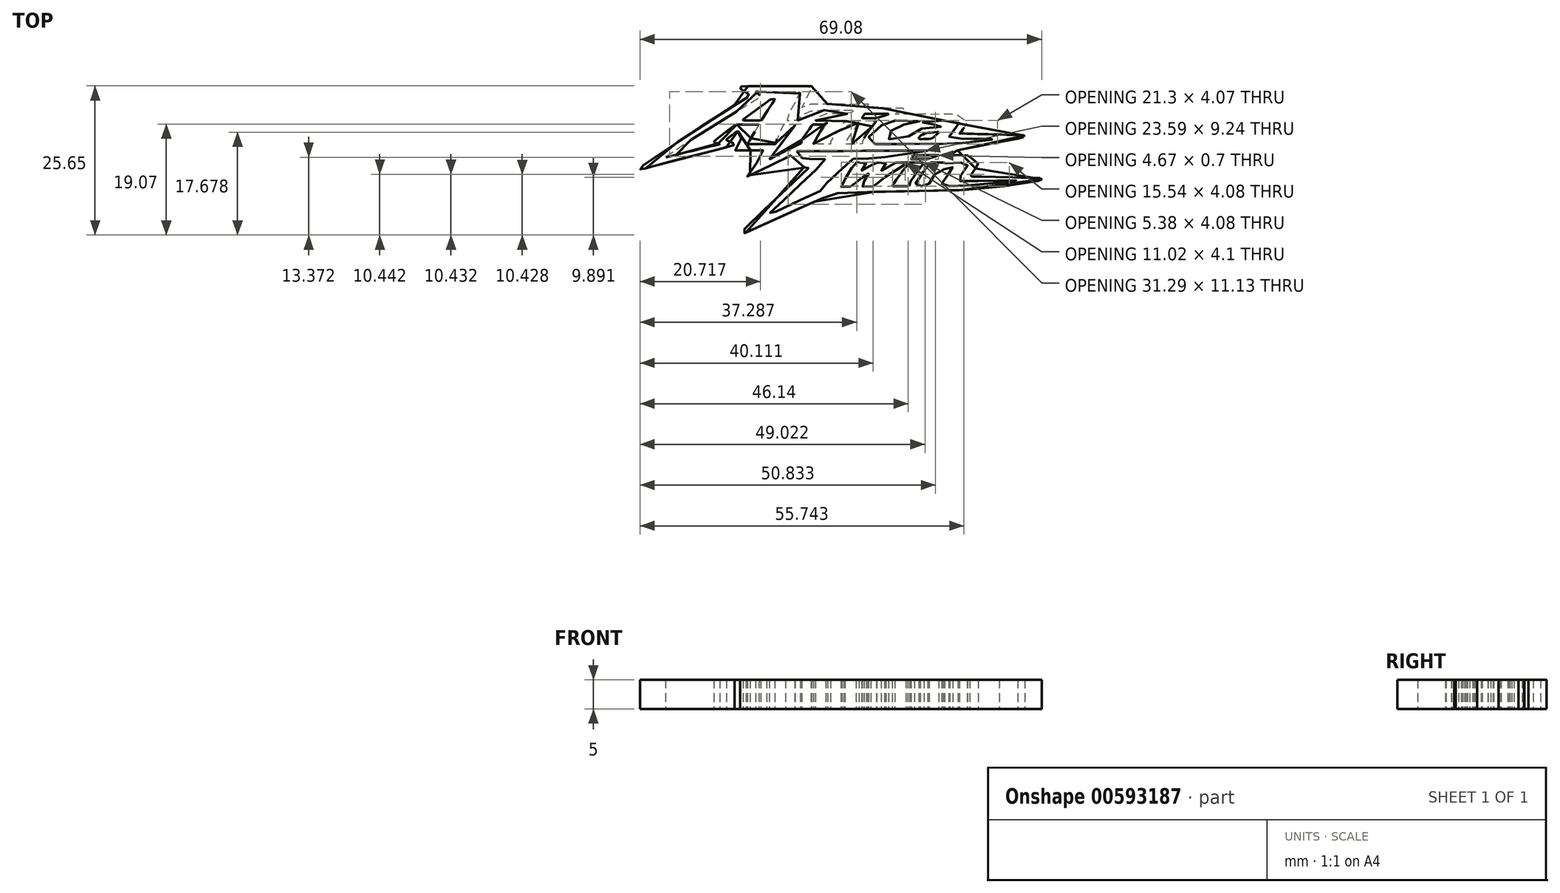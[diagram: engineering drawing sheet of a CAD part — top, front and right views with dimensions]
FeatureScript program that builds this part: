
annotation { "Feature Type Name" : "Feature", "Feature Type Description" : "" }
export const myFeature = defineFeature(function(context is Context, id is Id, definition is map)
    precondition{}
    {
        {
            var Q0;
            Q0=qCreatedBy(makeId("Top.planeOp"),FACE);
            var sketch = newSketch(context, id + "F0", { "sketchPlane" : qUnion([Q0])});
            skFitSpline(sketch, "E0", {"points": [v(-31.44, 20.71) * mm, v(-28.3, 20.77) * mm, v(-24.77, 20.79) * mm, v(-21.15, 20.83) * mm, v(-17.69, 20.85) * mm, v(-13.86, 20.87) * mm, v(-10.72, 20.85) * mm, v(-9.64, 20.77) * mm, v(-9.44, 20.67) * mm, v(-9.36, 20.45) * mm, v(-9.71, 19.84) * mm, v(-10.66, 17.85) * mm, v(-11.86, 15.37) * mm, v(-12.62, 13.83) * mm, v(-12.87, 13.46) * mm, v(-12.36, 13.66) * mm, v(-10.48, 14.38) * mm, v(-9.76, 14.62) * mm, v(-8.3, 14.67) * mm, v(-0.15, 14.62) * mm, v(8.5, 14.6) * mm, v(10.43, 14.62) * mm, v(10.86, 14.5) * mm, v(10.52, 14.24) * mm, v(9.13, 13.52) * mm, v(8.62, 13.24) * mm, v(9.3, 13.23) * mm, v(13.38, 13.2) * mm, v(17.6, 13.21) * mm, v(21.22, 13.2) * mm, v(22.36, 13.21) * mm, v(22.72, 13.17) * mm, v(22.9, 13.05) * mm, v(22.8, 12.92) * mm, v(22, 12.5) * mm, v(19.52, 11.38) * mm, v(19.17, 11.22) * mm, v(19.52, 11.18) * mm, v(21.42, 11.2) * mm, v(27.58, 11.15) * mm, v(35.7, 11.2) * mm, v(39.4, 11.2) * mm, v(39.96, 11.2) * mm, v(40.45, 11.02) * mm, v(41.07, 10.67) * mm, v(43.51, 8.93) * mm, v(43.88, 8.62) * mm, v(44.1, 8.35) * mm, v(44.07, 8.16) * mm, v(43.88, 7.78) * mm, v(43.2, 6.82) * mm, v(41.7, 4.75) * mm, v(41.4, 4.44) * mm, v(41.8, 4.44) * mm, v(46.51, 4.34) * mm, v(54.03, 4.15) * mm, v(62.87, 3.9) * mm, v(63.5, 3.86) * mm, v(63.75, 3.7) * mm, v(63.8, 3.5) * mm, v(63.56, 3.27) * mm, v(62.78, 3.02) * mm, v(61.33, 2.68) * mm, v(50.17, 0.51) * mm, v(48.29, 0.16) * mm, v(43.82, -0.7) * mm, v(41.17, -1.17) * mm, v(40.71, -1.31) * mm, v(40.3, -1.52) * mm, v(38.4, -2.7) * mm, v(38.08, -2.95) * mm, v(38.48, -2.96) * mm, v(42.95, -2.96) * mm, v(43.87, -3) * mm, v(44.42, -3.15) * mm, v(45.17, -3.73) * mm, v(47.66, -5.83) * mm, v(47.85, -6) * mm, v(47.88, -6.2) * mm, v(47.65, -6.53) * mm, v(45.18, -9.97) * mm, v(44.95, -10.32) * mm, v(45.44, -10.34) * mm, v(49.6, -10.42) * mm, v(60.85, -10.66) * mm, v(68.92, -10.88) * mm, v(69.35, -10.9) * mm, v(69.58, -11.06) * mm, v(69.63, -11.3) * mm, v(69.4, -11.5) * mm, v(68.72, -11.77) * mm, v(67.84, -11.94) * mm, v(61.37, -13.03) * mm, v(54.69, -13.9) * mm, v(46.25, -14.7) * mm, v(39.74, -15.1) * mm, v(35.06, -15.2) * mm, v(29.92, -15.28) * mm, v(24.8, -15.36) * mm, v(22.23, -15.43) * mm, v(14.78, -15.56) * mm, v(7.73, -15.76) * mm, v(1.76, -15.96) * mm, v(-0.16, -16.08) * mm, v(-1.23, -16.17) * mm, v(-1.7, -16.22) * mm, v(-2.2, -16.36) * mm, v(-3.15, -16.73) * mm, v(-5.36, -17.68) * mm, v(-8.55, -19) * mm, v(-11.16, -20.13) * mm, v(-15.96, -22.24) * mm, v(-19.22, -23.72) * mm, v(-24.73, -26.23) * mm, v(-29.57, -28.5) * mm, v(-31.83, -29.52) * mm, v(-33.6, -30.36) * mm, v(-33.79, -30.44) * mm, v(-33.93, -30.42) * mm, v(-34.06, -30.3) * mm, v(-34.08, -30.09) * mm, v(-33.96, -29.86) * mm, v(-33.08, -28.95) * mm, v(-30.44, -26.24) * mm, v(-27.52, -23.44) * mm, v(-24.82, -20.86) * mm, v(-21.12, -17.38) * mm, v(-17.92, -14.4) * mm, v(-14.38, -11.08) * mm, v(-11, -7.9) * mm, v(-9.75, -6.67) * mm, v(-9.62, -6.52) * mm, v(-9.85, -6.53) * mm, v(-10.86, -6.51) * mm, v(-10.98, -6.5) * mm, v(-11.63, -6.92) * mm, v(-11.95, -7.17) * mm, v(-12.1, -7.28) * mm, v(-12.24, -7.26) * mm, v(-12.64, -6.9) * mm, v(-15.8, -3.99) * mm, v(-16.66, -3.2) * mm, v(-16.75, -3.13) * mm, v(-16.94, -3.2) * mm, v(-19.02, -4.23) * mm, v(-21.54, -5.46) * mm, v(-26.34, -7.81) * mm, v(-30.32, -9.78) * mm, v(-31.48, -10.3) * mm, v(-31.67, -10.36) * mm, v(-31.85, -10.36) * mm, v(-31.94, -10.3) * mm, v(-32.02, -10.18) * mm, v(-31.91, -9.98) * mm, v(-31.16, -9.08) * mm, v(-27.72, -4.86) * mm, v(-25.69, -2.27) * mm, v(-25.03, -1.4) * mm, v(-24.98, -1.27) * mm, v(-25.27, -1.27) * mm, v(-30.34, -1.33) * mm, v(-34.83, -1.37) * mm, v(-35.61, -1.39) * mm, v(-35.8, -1.35) * mm, v(-35.92, -1.19) * mm, v(-35.92, -0.93) * mm, v(-35.79, -0.6) * mm, v(-35.04, 0.69) * mm, v(-33.92, 2.35) * mm, v(-32.9, 3.85) * mm, v(-31.97, 5.16) * mm, v(-31.97, 5.22) * mm, v(-32.3, 5.21) * mm, v(-34.88, 5.21) * mm, v(-34.96, 5.2) * mm, v(-35.2, 5.11) * mm, v(-36.44, 4.2) * mm, v(-38.05, 2.99) * mm, v(-38.72, 2.42) * mm, v(-38.81, 2.3) * mm, v(-38.79, 2.2) * mm, v(-38.64, 2.13) * mm, v(-38.37, 2) * mm, v(-36.75, 1.34) * mm, v(-36.2, 1.05) * mm, v(-35.96, 0.86) * mm, v(-35.85, 0.75) * mm, v(-35.93, 0.63) * mm, v(-36.35, 0.46) * mm, v(-37.36, 0.16) * mm, v(-39.12, -0.35) * mm, v(-42.53, -1.26) * mm, v(-47.35, -2.49) * mm, v(-52.88, -3.85) * mm, v(-58.58, -5.28) * mm, v(-64.61, -6.93) * mm, v(-67.43, -7.8) * mm, v(-67.74, -7.88) * mm, v(-68.03, -7.92) * mm, v(-68.31, -7.88) * mm, v(-68.5, -7.72) * mm, v(-68.5, -7.48) * mm, v(-68.17, -7.1) * mm, v(-67.4, -6.57) * mm, v(-64.48, -4.56) * mm, v(-61.76, -2.71) * mm, v(-58.36, -0.4) * mm, v(-55.05, 1.82) * mm, v(-52.23, 3.7) * mm, v(-49.26, 5.65) * mm, v(-46.62, 7.37) * mm, v(-43.48, 9.42) * mm, v(-40.62, 11.22) * mm, v(-37.84, 13) * mm, v(-34.36, 15.19) * mm, v(-31.23, 17.12) * mm, v(-30.7, 17.45) * mm, v(-30.59, 17.53) * mm, v(-30.7, 17.64) * mm, v(-31.88, 18.45) * mm, v(-33.47, 19.51) * mm, v(-34.2, 20.02) * mm, v(-34.3, 20.16) * mm, v(-34.33, 20.32) * mm, v(-34.21, 20.45) * mm, v(-33.86, 20.55) * mm, v(-33.08, 20.64) * mm, v(-32.38, 20.68) * mm, v(-31.44, 20.71) * mm]});
            skFitSpline(sketch, "E1", {"points": [v(-27.94, 18.83) * mm, v(-25.36, 18.85) * mm, v(-22.64, 18.83) * mm, v(-20.72, 18.82) * mm, v(-18.67, 18.83) * mm, v(-15.9, 18.83) * mm, v(-14.1, 18.83) * mm, v(-13.7, 18.83) * mm, v(-13.59, 18.81) * mm, v(-13.4, 18.65) * mm, v(-13.37, 18.58) * mm, v(-13.39, 18.45) * mm, v(-13.7, 17.85) * mm, v(-14.8, 15.8) * mm, v(-15.84, 13.94) * mm, v(-17.05, 11.71) * mm, v(-17.96, 9.93) * mm, v(-18.38, 9.15) * mm, v(-18.43, 9.04) * mm, v(-18.36, 8.98) * mm, v(-18.19, 8.98) * mm, v(-16.4, 8.98) * mm, v(-14.38, 9) * mm, v(-14.13, 9) * mm, v(-14, 9) * mm, v(-13.85, 9.16) * mm, v(-13.33, 9.76) * mm, v(-12.75, 10.5) * mm, v(-12.45, 10.91) * mm, v(-12.36, 11.02) * mm, v(-12.14, 11.15) * mm, v(-11.18, 11.59) * mm, v(-10.62, 11.83) * mm, v(-9.52, 12.26) * mm, v(-9.14, 12.38) * mm, v(-8.8, 12.46) * mm, v(-8.18, 12.48) * mm, v(-6.37, 12.48) * mm, v(-3.07, 12.5) * mm, v(0.47, 12.48) * mm, v(4, 12.5) * mm, v(5.57, 12.5) * mm, v(5.7, 12.47) * mm, v(5.77, 12.4) * mm, v(5.78, 12.33) * mm, v(5.63, 12.27) * mm, v(5.55, 12.22) * mm, v(4.72, 11.87) * mm, v(3.96, 11.55) * mm, v(3.4, 11.36) * mm, v(3.14, 11.28) * mm, v(2.72, 11.26) * mm, v(1.7, 11.25) * mm, v(-1.97, 11.24) * mm, v(-4.14, 11.26) * mm, v(-4.41, 11.24) * mm, v(-4.77, 11.17) * mm, v(-5.2, 10.98) * mm, v(-5.83, 10.72) * mm, v(-6.38, 10.48) * mm, v(-6.7, 10.32) * mm, v(-7.08, 10.03) * mm, v(-7.67, 9.55) * mm, v(-8.12, 9.15) * mm, v(-8.16, 9.05) * mm, v(-8.07, 8.98) * mm, v(-7.9, 9) * mm, v(-5.92, 9) * mm, v(-2.75, 8.97) * mm, v(0.26, 8.98) * mm, v(1.36, 8.99) * mm, v(1.5, 8.97) * mm, v(1.57, 8.94) * mm, v(1.6, 8.87) * mm, v(1.57, 8.8) * mm, v(1.47, 8.68) * mm, v(1.1, 8.12) * mm, v(1.03, 8.03) * mm, v(1.1, 7.95) * mm, v(1.2, 7.98) * mm, v(1.46, 8.12) * mm, v(2.51, 8.65) * mm, v(3.07, 8.87) * mm, v(3.35, 8.95) * mm, v(3.77, 8.97) * mm, v(5.54, 8.99) * mm, v(7.3, 8.97) * mm, v(9.54, 8.98) * mm, v(12.54, 8.99) * mm, v(12.68, 8.98) * mm, v(12.77, 8.95) * mm, v(12.82, 8.88) * mm, v(12.8, 8.83) * mm, v(12.7, 8.7) * mm, v(12.39, 8.3) * mm, v(11.56, 7.18) * mm, v(10.72, 6) * mm, v(9.85, 4.83) * mm, v(9.03, 3.65) * mm, v(8.33, 2.51) * mm, v(8.12, 2.16) * mm, v(7.97, 1.78) * mm, v(7.9, 1.55) * mm, v(7.9, 1.26) * mm, v(7.92, 1.1) * mm, v(7.96, 1.01) * mm, v(7.95, 0.92) * mm, v(7.88, 0.85) * mm, v(7.64, 0.85) * mm, v(7.26, 0.86) * mm, v(5.58, 0.85) * mm, v(4, 0.85) * mm, v(2.88, 0.84) * mm, v(2.23, 0.83) * mm, v(2.14, 0.87) * mm, v(2.05, 0.92) * mm, v(2, 1) * mm, v(2, 1.11) * mm, v(2.11, 1.26) * mm, v(2.32, 1.6) * mm, v(3.29, 3.02) * mm, v(4.07, 4.21) * mm, v(4.93, 5.49) * mm, v(5.7, 6.66) * mm, v(6.27, 7.5) * mm, v(6.62, 8.04) * mm, v(6.77, 8.25) * mm, v(6.84, 8.35) * mm, v(6.8, 8.39) * mm, v(6.75, 8.36) * mm, v(6.6, 8.3) * mm, v(6.12, 8.06) * mm, v(5.7, 7.86) * mm, v(5.39, 7.68) * mm, v(5.17, 7.57) * mm, v(4.7, 7.51) * mm, v(4.02, 7.45) * mm, v(3.55, 7.4) * mm, v(3.34, 7.36) * mm, v(3.18, 7.3) * mm, v(2.6, 7.04) * mm, v(1.12, 6.3) * mm, v(-0.07, 5.6) * mm, v(-0.36, 5.41) * mm, v(-0.58, 5.19) * mm, v(-0.91, 4.83) * mm, v(-1.73, 3.65) * mm, v(-2.5, 2.48) * mm, v(-2.83, 1.87) * mm, v(-2.94, 1.49) * mm, v(-2.97, 1.2) * mm, v(-2.94, 0.93) * mm, v(-2.93, 0.86) * mm, v(-3.01, 0.83) * mm, v(-3.3, 0.84) * mm, v(-4.13, 0.84) * mm, v(-6.48, 0.84) * mm, v(-8.4, 0.84) * mm, v(-8.54, 0.85) * mm, v(-8.67, 0.9) * mm, v(-8.74, 0.95) * mm, v(-8.78, 1.04) * mm, v(-8.74, 1.15) * mm, v(-8.6, 1.33) * mm, v(-8.25, 1.87) * mm, v(-7.37, 3.17) * mm, v(-6.3, 4.76) * mm, v(-5.43, 6.05) * mm, v(-4.42, 7.53) * mm, v(-4.17, 7.86) * mm, v(-3.95, 8.14) * mm, v(-3.91, 8.2) * mm, v(-3.93, 8.22) * mm, v(-3.98, 8.25) * mm, v(-4.12, 8.19) * mm, v(-4.58, 7.97) * mm, v(-4.8, 7.86) * mm, v(-5.04, 7.75) * mm, v(-5.15, 7.68) * mm, v(-5.28, 7.57) * mm, v(-5.41, 7.57) * mm, v(-6.5, 7.58) * mm, v(-7.44, 7.6) * mm, v(-8.45, 7.58) * mm, v(-8.72, 7.59) * mm, v(-8.86, 7.58) * mm, v(-9.02, 7.53) * mm, v(-9.2, 7.4) * mm, v(-9.4, 7.17) * mm, v(-10.12, 6.14) * mm, v(-10.87, 5.13) * mm, v(-12.03, 3.51) * mm, v(-12.67, 2.61) * mm, v(-12.94, 2.1) * mm, v(-13, 1.78) * mm, v(-12.98, 1.39) * mm, v(-12.98, 1.24) * mm, v(-12.98, 1.18) * mm, v(-13.05, 1.12) * mm, v(-13.57, 0.85) * mm, v(-16.05, -0.34) * mm, v(-18.68, -1.62) * mm, v(-21.07, -2.85) * mm, v(-23.2, -4.06) * mm, v(-23.86, -4.42) * mm, v(-23.99, -4.46) * mm, v(-23.97, -4.38) * mm, v(-23.9, -4.3) * mm, v(-23.55, -3.86) * mm, v(-22.4, -2.47) * mm, v(-21.58, -1.48) * mm, v(-21.03, -0.75) * mm, v(-20.06, 0.46) * mm, v(-19.46, 1.23) * mm, v(-17.66, 3.63) * mm, v(-15.85, 6.13) * mm, v(-15.14, 7.15) * mm, v(-15.08, 7.24) * mm, v(-15.1, 7.37) * mm, v(-15.22, 7.48) * mm, v(-15.39, 7.55) * mm, v(-15.54, 7.59) * mm, v(-16.37, 7.58) * mm, v(-18.12, 7.59) * mm, v(-18.98, 7.59) * mm, v(-19.06, 7.6) * mm, v(-19.12, 7.57) * mm, v(-19.19, 7.46) * mm, v(-19.71, 6.32) * mm, v(-20.6, 4.39) * mm, v(-21.2, 3) * mm, v(-21.35, 2.6) * mm, v(-21.5, 2.03) * mm, v(-21.7, 1.2) * mm, v(-21.75, 1.05) * mm, v(-21.8, 0.96) * mm, v(-21.91, 0.89) * mm, v(-22.11, 0.86) * mm, v(-22.6, 0.87) * mm, v(-25.77, 0.85) * mm, v(-28.27, 0.82) * mm, v(-30.4, 0.78) * mm, v(-31.24, 0.76) * mm, v(-31.37, 0.78) * mm, v(-31.45, 0.84) * mm, v(-31.48, 0.93) * mm, v(-31.44, 1.05) * mm, v(-31.24, 1.34) * mm, v(-30.56, 2.5) * mm, v(-30.22, 3.09) * mm, v(-29.67, 4.03) * mm, v(-29.06, 4.98) * mm, v(-28.3, 6.24) * mm, v(-27.74, 7.1) * mm, v(-27.63, 7.3) * mm, v(-27.6, 7.44) * mm, v(-27.66, 7.53) * mm, v(-27.78, 7.57) * mm, v(-28.8, 7.57) * mm, v(-32.18, 7.55) * mm, v(-34.64, 7.59) * mm, v(-35.2, 7.6) * mm, v(-35.48, 7.55) * mm, v(-35.8, 7.42) * mm, v(-36.13, 7.21) * mm, v(-36.46, 6.95) * mm, v(-37.18, 6.43) * mm, v(-39.8, 4.34) * mm, v(-41.94, 2.73) * mm, v(-42.38, 2.35) * mm, v(-42.88, 1.92) * mm, v(-43.03, 1.74) * mm, v(-43.06, 1.59) * mm, v(-42.98, 1.45) * mm, v(-42.76, 1.34) * mm, v(-41.95, 1.15) * mm, v(-41.37, 1.02) * mm, v(-41.17, 0.92) * mm, v(-41.08, 0.85) * mm, v(-41.08, 0.78) * mm, v(-41.16, 0.73) * mm, v(-41.47, 0.67) * mm, v(-41.8, 0.57) * mm, v(-44.01, 0.07) * mm, v(-45.43, -0.27) * mm, v(-48.03, -0.9) * mm, v(-51.88, -1.85) * mm, v(-54.82, -2.56) * mm, v(-58.1, -3.36) * mm, v(-59.13, -3.63) * mm, v(-59.46, -3.7) * mm, v(-59.64, -3.68) * mm, v(-59.65, -3.61) * mm, v(-59.58, -3.5) * mm, v(-59.4, -3.34) * mm, v(-58.34, -2.59) * mm, v(-56.94, -1.67) * mm, v(-54.92, -0.34) * mm, v(-53.9, 0.34) * mm, v(-51.67, 1.76) * mm, v(-49.53, 3.14) * mm, v(-48.87, 3.58) * mm, v(-48.73, 3.67) * mm, v(-47.04, 4.75) * mm, v(-44.1, 6.6) * mm, v(-41.55, 8.22) * mm, v(-38.39, 10.15) * mm, v(-35.9, 11.7) * mm, v(-33.5, 13.18) * mm, v(-30.87, 14.8) * mm, v(-27.86, 16.62) * mm, v(-26.98, 17.22) * mm, v(-26.93, 17.35) * mm, v(-26.94, 17.46) * mm, v(-27.02, 17.57) * mm, v(-27.47, 17.84) * mm, v(-27.98, 18.15) * mm, v(-28.6, 18.54) * mm, v(-28.65, 18.63) * mm, v(-28.66, 18.74) * mm, v(-28.59, 18.83) * mm, v(-28.36, 18.84) * mm, v(-27.94, 18.83) * mm]});
            skFitSpline(sketch, "E2", {"points": [v(-22.35, 15.82) * mm, v(-22.84, 15.12) * mm, v(-23.43, 14.18) * mm, v(-24.2, 13.02) * mm, v(-24.91, 11.9) * mm, v(-26, 10.2) * mm, v(-26.5, 9.37) * mm, v(-26.57, 9.25) * mm, v(-26.7, 9.13) * mm, v(-26.97, 9) * mm, v(-27.15, 8.98) * mm, v(-27.78, 8.98) * mm, v(-30.38, 8.98) * mm, v(-32.52, 8.99) * mm, v(-32.62, 8.99) * mm, v(-32.84, 9) * mm, v(-32.96, 9.05) * mm, v(-33.05, 9.11) * mm, v(-33.07, 9.23) * mm, v(-33, 9.36) * mm, v(-32.83, 9.5) * mm, v(-32.07, 10.06) * mm, v(-30.65, 11.06) * mm, v(-29.08, 12.22) * mm, v(-28.27, 12.82) * mm, v(-26.87, 13.82) * mm, v(-25.71, 14.67) * mm, v(-24.21, 15.76) * mm, v(-23.77, 16.09) * mm, v(-23.6, 16.2) * mm, v(-23.35, 16.27) * mm, v(-23.1, 16.3) * mm, v(-22.62, 16.3) * mm, v(-22.22, 16.32) * mm, v(-22.13, 16.28) * mm, v(-22.11, 16.21) * mm, v(-22.15, 16.15) * mm, v(-22.25, 16) * mm, v(-22.35, 15.82) * mm]});
            skFitSpline(sketch, "E3", {"points": [v(12, 11.25) * mm, v(14.22, 11.25) * mm, v(16.62, 11.24) * mm, v(16.78, 11.24) * mm, v(16.86, 11.21) * mm, v(16.96, 11.13) * mm, v(16.95, 11.09) * mm, v(16.84, 11.03) * mm, v(16.26, 10.83) * mm, v(14.13, 10.16) * mm, v(13.26, 9.87) * mm, v(13.01, 9.8) * mm, v(12.88, 9.79) * mm, v(12.62, 9.75) * mm, v(12, 9.74) * mm, v(9.53, 9.74) * mm, v(8.25, 9.74) * mm, v(8.1, 9.75) * mm, v(8, 9.8) * mm, v(7.93, 9.9) * mm, v(7.96, 10) * mm, v(8.08, 10.19) * mm, v(8.3, 10.52) * mm, v(8.66, 11.04) * mm, v(8.75, 11.14) * mm, v(8.92, 11.2) * mm, v(9.11, 11.22) * mm, v(9.68, 11.23) * mm, v(12, 11.25) * mm]});
            skFitSpline(sketch, "E4", {"points": [v(19.36, 8.99) * mm, v(22.68, 8.97) * mm, v(26.98, 8.98) * mm, v(27.74, 8.98) * mm, v(27.87, 8.95) * mm, v(27.9, 8.9) * mm, v(27.9, 8.85) * mm, v(27.81, 8.79) * mm, v(26.72, 8.05) * mm, v(26.31, 7.8) * mm, v(26.14, 7.7) * mm, v(25.95, 7.64) * mm, v(25.68, 7.6) * mm, v(25.22, 7.58) * mm, v(23.34, 7.58) * mm, v(22.34, 7.58) * mm, v(22.07, 7.58) * mm, v(21.9, 7.56) * mm, v(21.57, 7.43) * mm, v(20.7, 7.11) * mm, v(19.5, 6.6) * mm, v(19.23, 6.46) * mm, v(18.91, 6.25) * mm, v(18.35, 5.78) * mm, v(16.43, 4.07) * mm, v(15.81, 3.42) * mm, v(15.68, 3.27) * mm, v(15.64, 3.16) * mm, v(15.67, 3) * mm, v(15.77, 2.85) * mm, v(16.02, 2.67) * mm, v(16.3, 2.56) * mm, v(16.65, 2.52) * mm, v(17.73, 2.53) * mm, v(21.55, 2.52) * mm, v(22.6, 2.53) * mm, v(22.94, 2.53) * mm, v(23, 2.53) * mm, v(23.05, 2.6) * mm, v(23.41, 3.02) * mm, v(23.63, 3.26) * mm, v(24.59, 4.23) * mm, v(25.3, 4.9) * mm, v(25.69, 5.2) * mm, v(25.97, 5.35) * mm, v(26.75, 5.64) * mm, v(27.39, 5.85) * mm, v(28.23, 6.08) * mm, v(28.93, 6.15) * mm, v(29.7, 6.23) * mm, v(31.7, 6.4) * mm, v(33.63, 6.54) * mm, v(34.2, 6.6) * mm, v(34.7, 6.66) * mm, v(35.26, 6.83) * mm, v(35.67, 7.05) * mm, v(36.07, 7.23) * mm, v(36.27, 7.4) * mm, v(36.3, 7.48) * mm, v(36.3, 7.54) * mm, v(36.25, 7.57) * mm, v(36.1, 7.57) * mm, v(34.31, 7.56) * mm, v(32.6, 7.56) * mm, v(30.43, 7.56) * mm, v(28.46, 7.56) * mm, v(28.03, 7.55) * mm, v(27.98, 7.56) * mm, v(27.91, 7.6) * mm, v(27.86, 7.67) * mm, v(27.85, 7.73) * mm, v(27.9, 7.8) * mm, v(28.04, 7.9) * mm, v(28.89, 8.5) * mm, v(29.46, 8.87) * mm, v(29.62, 8.94) * mm, v(29.72, 8.98) * mm, v(29.84, 8.99) * mm, v(30.41, 9) * mm, v(32.93, 9) * mm, v(35.39, 8.99) * mm, v(38.86, 8.99) * mm, v(39.63, 8.98) * mm, v(39.87, 8.97) * mm, v(40.04, 8.93) * mm, v(40.22, 8.87) * mm, v(40.42, 8.75) * mm, v(41.05, 8.3) * mm, v(41.22, 8.16) * mm, v(41.28, 8.07) * mm, v(41.3, 7.97) * mm, v(41.27, 7.87) * mm, v(41.14, 7.68) * mm, v(41.01, 7.5) * mm, v(40.1, 6.26) * mm, v(39.1, 4.97) * mm, v(38.1, 3.7) * mm, v(37.82, 3.3) * mm, v(37.74, 3.21) * mm, v(37.71, 3.11) * mm, v(37.74, 3.03) * mm, v(37.83, 2.93) * mm, v(38.07, 2.8) * mm, v(38.36, 2.63) * mm, v(38.56, 2.56) * mm, v(38.7, 2.54) * mm, v(39.3, 2.56) * mm, v(41.81, 2.58) * mm, v(44.71, 2.63) * mm, v(47.11, 2.67) * mm, v(49.35, 2.7) * mm, v(51.41, 2.72) * mm, v(52.93, 2.75) * mm, v(54.17, 2.77) * mm, v(54.89, 2.79) * mm, v(54.96, 2.8) * mm, v(55.02, 2.78) * mm, v(55.05, 2.74) * mm, v(55.03, 2.71) * mm, v(54.96, 2.68) * mm, v(54.82, 2.66) * mm, v(53.2, 2.43) * mm, v(51.02, 2.17) * mm, v(48.66, 1.9) * mm, v(45.26, 1.54) * mm, v(41.9, 1.17) * mm, v(39.22, 0.86) * mm, v(38.78, 0.84) * mm, v(36.51, 0.83) * mm, v(35.17, 0.83) * mm, v(34.5, 0.86) * mm, v(34.22, 0.9) * mm, v(34.05, 0.96) * mm, v(33.78, 1.18) * mm, v(33.61, 1.38) * mm, v(33.52, 1.52) * mm, v(33.42, 1.69) * mm, v(33.38, 1.76) * mm, v(33.36, 1.75) * mm, v(33.27, 1.66) * mm, v(32.95, 1.44) * mm, v(32.42, 1.15) * mm, v(32.03, 0.98) * mm, v(31.5, 0.89) * mm, v(30.58, 0.84) * mm, v(28.38, 0.84) * mm, v(25.63, 0.85) * mm, v(23.37, 0.85) * mm, v(19.81, 0.85) * mm, v(16.57, 0.85) * mm, v(13.2, 0.84) * mm, v(12.09, 0.83) * mm, v(11.79, 0.85) * mm, v(11.35, 1) * mm, v(10.86, 1.32) * mm, v(10.16, 2.03) * mm, v(9.82, 2.45) * mm, v(9.75, 2.63) * mm, v(9.75, 2.76) * mm, v(9.81, 2.9) * mm, v(9.97, 3.08) * mm, v(10.5, 3.63) * mm, v(11.11, 4.23) * mm, v(11.88, 4.94) * mm, v(13, 5.95) * mm, v(14.06, 6.9) * mm, v(14.34, 7.11) * mm, v(14.56, 7.3) * mm, v(15.03, 7.59) * mm, v(15.46, 7.77) * mm, v(16.45, 8.18) * mm, v(17.81, 8.69) * mm, v(18.25, 8.85) * mm, v(18.6, 8.95) * mm, v(18.93, 8.99) * mm, v(19.36, 8.99) * mm]});
            skFitSpline(sketch, "E5", {"points": [v(30.67, 4.75) * mm, v(32.06, 4.83) * mm, v(33.57, 4.98) * mm, v(34.1, 5) * mm, v(34.25, 4.98) * mm, v(34.3, 4.94) * mm, v(34.3, 4.86) * mm, v(34.18, 4.73) * mm, v(33.6, 4.16) * mm, v(32.93, 3.51) * mm, v(32.56, 3.19) * mm, v(32.18, 2.95) * mm, v(31.7, 2.76) * mm, v(31.22, 2.65) * mm, v(30.5, 2.56) * mm, v(28.92, 2.54) * mm, v(27.99, 2.53) * mm, v(27.72, 2.58) * mm, v(27.49, 2.74) * mm, v(27.38, 2.83) * mm, v(27.35, 2.9) * mm, v(27.4, 3.02) * mm, v(27.57, 3.28) * mm, v(27.68, 3.42) * mm, v(27.96, 3.64) * mm, v(28.47, 3.97) * mm, v(29.04, 4.3) * mm, v(29.6, 4.54) * mm, v(30.1, 4.68) * mm, v(30.67, 4.75) * mm]});
            skFitSpline(sketch, "E6", {"points": [v(-14.6, -1.57) * mm, v(-11.2, -1.57) * mm, v(-8.48, -1.56) * mm, v(-4.15, -1.55) * mm, v(-0.76, -1.54) * mm, v(2.28, -1.52) * mm, v(4.75, -1.5) * mm, v(6.58, -1.5) * mm, v(8.88, -1.5) * mm, v(11.94, -1.5) * mm, v(14.7, -1.47) * mm, v(17.8, -1.44) * mm, v(22.1, -1.44) * mm, v(25.9, -1.42) * mm, v(29.15, -1.42) * mm, v(29.99, -1.41) * mm, v(30.42, -1.4) * mm, v(30.5, -1.42) * mm, v(30.5, -1.45) * mm, v(30.4, -1.48) * mm, v(28.76, -1.77) * mm, v(25.05, -2.3) * mm, v(21.95, -2.78) * mm, v(17.9, -3.34) * mm, v(13.88, -3.92) * mm, v(12.93, -4.08) * mm, v(12.07, -4.13) * mm, v(10.14, -4.11) * mm, v(8.64, -4.14) * mm, v(5.74, -4.19) * mm, v(5.16, -4.21) * mm, v(4.9, -4.26) * mm, v(4.63, -4.38) * mm, v(4.25, -4.64) * mm, v(3.5, -5.28) * mm, v(2.2, -6.52) * mm, v(0.46, -8.22) * mm, v(-1.37, -9.96) * mm, v(-3.6, -12.02) * mm, v(-5.55, -13.84) * mm, v(-5.8, -14.14) * mm, v(-6.04, -14.49) * mm, v(-6.16, -14.84) * mm, v(-6.29, -15.13) * mm, v(-6.33, -15.2) * mm, v(-6.42, -15.26) * mm, v(-6.73, -15.42) * mm, v(-10.19, -16.97) * mm, v(-13.51, -18.47) * mm, v(-17.5, -20.35) * mm, v(-21.58, -22.33) * mm, v(-23.28, -23.15) * mm, v(-23.75, -23.37) * mm, v(-23.85, -23.4) * mm, v(-24, -23.4) * mm, v(-24.06, -23.38) * mm, v(-24.08, -23.3) * mm, v(-24.05, -23.2) * mm, v(-23.92, -23.03) * mm, v(-23.24, -22.4) * mm, v(-21.57, -20.8) * mm, v(-20.09, -19.4) * mm, v(-17.6, -17.07) * mm, v(-15.2, -14.85) * mm, v(-13.02, -12.8) * mm, v(-10.94, -10.93) * mm, v(-8.92, -9.02) * mm, v(-6.32, -6.58) * mm, v(-4.75, -5.1) * mm, v(-4.58, -4.88) * mm, v(-4.54, -4.78) * mm, v(-4.56, -4.66) * mm, v(-4.85, -4.45) * mm, v(-5.14, -4.28) * mm, v(-5.25, -4.23) * mm, v(-5.49, -4.24) * mm, v(-7, -4.24) * mm, v(-10.43, -4.22) * mm, v(-11.54, -4.22) * mm, v(-11.66, -4.23) * mm, v(-11.73, -4.25) * mm, v(-11.84, -4.36) * mm, v(-11.98, -4.47) * mm, v(-12.05, -4.5) * mm, v(-12.1, -4.49) * mm, v(-12.23, -4.4) * mm, v(-12.56, -4.1) * mm, v(-14.16, -2.73) * mm, v(-15.13, -1.84) * mm, v(-15.2, -1.76) * mm, v(-15.23, -1.66) * mm, v(-15.19, -1.6) * mm, v(-15.1, -1.56) * mm, v(-14.6, -1.57) * mm]});
            skFitSpline(sketch, "E7", {"points": [v(6.07, -5.46) * mm, v(8.68, -5.48) * mm, v(9.15, -5.5) * mm, v(9.27, -5.5) * mm, v(9.33, -5.53) * mm, v(9.36, -5.6) * mm, v(9.32, -5.69) * mm, v(9.2, -5.9) * mm, v(8.52, -6.99) * mm, v(8.03, -7.79) * mm, v(7.8, -8.15) * mm, v(7.77, -8.25) * mm, v(7.78, -8.35) * mm, v(7.86, -8.41) * mm, v(8, -8.35) * mm, v(8.57, -7.98) * mm, v(9.33, -7.52) * mm, v(10.97, -6.48) * mm, v(11.65, -6.02) * mm, v(12.27, -5.64) * mm, v(12.43, -5.55) * mm, v(12.66, -5.5) * mm, v(13.2, -5.47) * mm, v(14, -5.48) * mm, v(15.85, -5.48) * mm, v(16.05, -5.52) * mm, v(16.1, -5.56) * mm, v(16.14, -5.64) * mm, v(16.06, -5.78) * mm, v(15.87, -6.06) * mm, v(15.23, -7.14) * mm, v(14.78, -7.84) * mm, v(14.57, -8.2) * mm, v(14.51, -8.3) * mm, v(14.52, -8.4) * mm, v(14.6, -8.43) * mm, v(14.8, -8.31) * mm, v(15.52, -7.85) * mm, v(16.5, -7.26) * mm, v(17.29, -6.78) * mm, v(18.2, -6.26) * mm, v(19, -5.76) * mm, v(19.28, -5.58) * mm, v(19.41, -5.51) * mm, v(19.6, -5.48) * mm, v(19.84, -5.48) * mm, v(23.1, -5.47) * mm, v(23.46, -5.48) * mm, v(23.52, -5.48) * mm, v(23.56, -5.53) * mm, v(23.5, -5.58) * mm, v(23.22, -5.77) * mm, v(22.43, -6.3) * mm, v(20.83, -7.31) * mm, v(19.24, -8.32) * mm, v(17.72, -9.29) * mm, v(15.52, -10.77) * mm, v(14.27, -11.65) * mm, v(13.88, -11.95) * mm, v(13.56, -12.26) * mm, v(13.28, -12.57) * mm, v(13.1, -12.83) * mm, v(12.97, -13.1) * mm, v(12.94, -13.32) * mm, v(12.93, -13.51) * mm, v(12.93, -13.56) * mm, v(12.88, -13.58) * mm, v(12.76, -13.6) * mm, v(11.73, -13.6) * mm, v(10.8, -13.63) * mm, v(9.54, -13.7) * mm, v(8.3, -13.72) * mm, v(7.96, -13.73) * mm, v(7.82, -13.7) * mm, v(7.72, -13.65) * mm, v(7.7, -13.58) * mm, v(7.71, -13.46) * mm, v(7.93, -13.07) * mm, v(8.34, -12.42) * mm, v(8.9, -11.42) * mm, v(9.36, -10.66) * mm, v(9.67, -10.16) * mm, v(9.96, -9.7) * mm, v(10.14, -9.4) * mm, v(10.18, -9.35) * mm, v(10.18, -9.32) * mm, v(10.15, -9.34) * mm, v(10.01, -9.41) * mm, v(9.36, -9.84) * mm, v(8.5, -10.42) * mm, v(7.48, -11.11) * mm, v(7, -11.48) * mm, v(6.18, -12.06) * mm, v(5.68, -12.42) * mm, v(5.4, -12.66) * mm, v(5.26, -12.88) * mm, v(5.14, -13.05) * mm, v(5.02, -13.34) * mm, v(4.95, -13.55) * mm, v(4.92, -13.66) * mm, v(4.86, -13.69) * mm, v(4.66, -13.7) * mm, v(3.26, -13.77) * mm, v(2.09, -13.86) * mm, v(1, -13.93) * mm, v(0.85, -13.91) * mm, v(0.75, -13.88) * mm, v(0.68, -13.81) * mm, v(0.66, -13.71) * mm, v(0.72, -13.57) * mm, v(0.86, -13.3) * mm, v(1.6, -12.07) * mm, v(2.29, -10.93) * mm, v(2.84, -10) * mm, v(3.3, -9.2) * mm, v(4.04, -7.98) * mm, v(4.69, -6.95) * mm, v(5.22, -6.06) * mm, v(5.58, -5.5) * mm, v(5.66, -5.47) * mm, v(5.84, -5.45) * mm, v(6.07, -5.46) * mm]});
            skFitSpline(sketch, "E8", {"points": [v(27.89, -3.02) * mm, v(30.66, -3.01) * mm, v(33.29, -3.01) * mm, v(34.05, -2.99) * mm, v(34.21, -3) * mm, v(34.21, -3.03) * mm, v(33.93, -3.12) * mm, v(32.8, -3.53) * mm, v(31.45, -3.98) * mm, v(30.54, -4.3) * mm, v(30.41, -4.35) * mm, v(30.27, -4.37) * mm, v(28.54, -4.4) * mm, v(26.16, -4.4) * mm, v(24.9, -4.4) * mm, v(24.83, -4.36) * mm, v(24.78, -4.29) * mm, v(24.81, -4.16) * mm, v(25.28, -3.56) * mm, v(25.66, -3.08) * mm, v(25.73, -3.02) * mm, v(25.8, -3) * mm, v(27.89, -3.02) * mm]});
            skFitSpline(sketch, "E9", {"points": [v(24.8, -5.5) * mm, v(28.52, -5.5) * mm, v(28.86, -5.5) * mm, v(29.01, -5.5) * mm, v(29.1, -5.54) * mm, v(29.14, -5.61) * mm, v(29.1, -5.7) * mm, v(28.82, -6.05) * mm, v(27.83, -7.4) * mm, v(26.59, -9.11) * mm, v(25.28, -10.96) * mm, v(24.71, -11.84) * mm, v(24.47, -12.25) * mm, v(24.3, -12.64) * mm, v(24.2, -12.98) * mm, v(24.23, -13.42) * mm, v(24.23, -13.54) * mm, v(24.23, -13.59) * mm, v(24.13, -13.6) * mm, v(22.42, -13.65) * mm, v(19.82, -13.68) * mm, v(18.58, -13.69) * mm, v(18.4, -13.66) * mm, v(18.33, -13.6) * mm, v(18.27, -13.5) * mm, v(18.3, -13.4) * mm, v(18.44, -13.2) * mm, v(19.41, -11.83) * mm, v(19.98, -11) * mm, v(21.08, -9.54) * mm, v(22.16, -8.03) * mm, v(23.26, -6.62) * mm, v(23.92, -5.86) * mm, v(24.17, -5.57) * mm, v(24.22, -5.5) * mm, v(24.3, -5.5) * mm, v(24.8, -5.5) * mm]});
            skFitSpline(sketch, "E10", {"points": [v(31.53, -5.5) * mm, v(33.25, -5.51) * mm, v(34.88, -5.5) * mm, v(35.52, -5.5) * mm, v(35.65, -5.5) * mm, v(35.77, -5.56) * mm, v(35.77, -5.62) * mm, v(35.68, -5.77) * mm, v(35.5, -6) * mm, v(35.4, -6.14) * mm, v(35.4, -6.2) * mm, v(35.44, -6.28) * mm, v(35.57, -6.25) * mm, v(35.9, -6.15) * mm, v(37.28, -5.67) * mm, v(37.62, -5.57) * mm, v(37.93, -5.51) * mm, v(38.46, -5.5) * mm, v(41.56, -5.5) * mm, v(42.63, -5.5) * mm, v(42.8, -5.51) * mm, v(43, -5.57) * mm, v(43.4, -5.86) * mm, v(44.09, -6.33) * mm, v(44.18, -6.43) * mm, v(44.22, -6.53) * mm, v(44.16, -6.65) * mm, v(43.75, -7.23) * mm, v(43.12, -8.14) * mm, v(42.08, -9.63) * mm, v(41.22, -10.8) * mm, v(40.87, -11.26) * mm, v(40.81, -11.36) * mm, v(40.83, -11.47) * mm, v(40.95, -11.6) * mm, v(41.2, -11.76) * mm, v(41.45, -11.87) * mm, v(41.79, -11.91) * mm, v(43.11, -11.9) * mm, v(46.35, -11.87) * mm, v(49.15, -11.83) * mm, v(51.56, -11.8) * mm, v(54.45, -11.79) * mm, v(56.8, -11.76) * mm, v(59.52, -11.7) * mm, v(61.18, -11.72) * mm, v(61.37, -11.73) * mm, v(61.44, -11.76) * mm, v(61.48, -11.8) * mm, v(61.46, -11.86) * mm, v(61.37, -11.91) * mm, v(61.07, -11.97) * mm, v(58.26, -12.25) * mm, v(55.58, -12.47) * mm, v(52.1, -12.74) * mm, v(48.76, -12.99) * mm, v(45.73, -13.22) * mm, v(42.7, -13.44) * mm, v(40.52, -13.6) * mm, v(39.03, -13.61) * mm, v(36.88, -13.6) * mm, v(36.7, -13.58) * mm, v(36.32, -13.48) * mm, v(35.7, -13.2) * mm, v(35.38, -13.01) * mm, v(35.32, -12.9) * mm, v(35.3, -12.8) * mm, v(35.38, -12.64) * mm, v(35.61, -12.3) * mm, v(36.07, -11.65) * mm, v(36.68, -10.79) * mm, v(37.42, -9.7) * mm, v(37.97, -8.93) * mm, v(38.58, -8.04) * mm, v(38.93, -7.57) * mm, v(39.04, -7.41) * mm, v(39.08, -7.28) * mm, v(39, -7.14) * mm, v(38.75, -7.06) * mm, v(38.34, -7.04) * mm, v(38, -7.02) * mm, v(37.72, -7.07) * mm, v(37.3, -7.26) * mm, v(36.37, -7.7) * mm, v(34.66, -8.42) * mm, v(33.8, -8.83) * mm, v(33.48, -9.02) * mm, v(33.25, -9.23) * mm, v(32.9, -9.63) * mm, v(32.06, -10.82) * mm, v(31.37, -11.84) * mm, v(31.1, -12.26) * mm, v(31, -12.56) * mm, v(30.96, -12.87) * mm, v(30.95, -13.3) * mm, v(30.94, -13.5) * mm, v(30.89, -13.57) * mm, v(30.79, -13.64) * mm, v(30.65, -13.66) * mm, v(29.9, -13.65) * mm, v(27.24, -13.66) * mm, v(26.11, -13.66) * mm, v(25.98, -13.64) * mm, v(25.88, -13.57) * mm, v(25.85, -13.47) * mm, v(25.9, -13.33) * mm, v(26.06, -13.08) * mm, v(26.73, -12.1) * mm, v(27.2, -11.4) * mm, v(28.14, -9.97) * mm, v(29.05, -8.62) * mm, v(30.39, -6.6) * mm, v(30.98, -5.7) * mm, v(31.1, -5.57) * mm, v(31.26, -5.53) * mm, v(31.53, -5.5) * mm]});
            skSolve(sketch);
        }
        {
            var Q0;
            Q0=makeQuery(id+"F0.imprint","IMPRINT",FACE,{"disambiguationData":[TD([[makeQuery(id+"F0.imprint","IMPRINT",EDGE,{"derivedFrom":sQuery(id+"F0.wireOp",EDGE,"E0")}),-1.0]])]});
            var Q1;
            Q1=makeQuery(id+"F0.imprint","IMPRINT",FACE,{"disambiguationData":[TD([[makeQuery(id+"F0.imprint","IMPRINT",EDGE,{"derivedFrom":sQuery(id+"F0.wireOp",EDGE,"E5")}),-1.0]])]});
            var Q2;
            Q2=makeQuery(id+"F0.imprint","IMPRINT",FACE,{"disambiguationData":[TD([[makeQuery(id+"F0.imprint","IMPRINT",EDGE,{"derivedFrom":sQuery(id+"F0.wireOp",EDGE,"E2")}),-1.0]])]});
            extrude(context, id + "F1", {"entities" : qUnion([Q0, Q1, Q2]), "depth" : 10 * mm, "offsetDistance" : 25 * mm});
        }
        {
            var Q0;
            Q0=makeQuery(id+"F1.opExtrude","SWEPT_BODY",BODY,{"disambiguationData":[OSD([sQuery(id+"F0.wireOp",EDGE,"E0"),sQuery(id+"F0.wireOp",EDGE,"E1"),sQuery(id+"F0.wireOp",EDGE,"E3"),sQuery(id+"F0.wireOp",EDGE,"E4"),sQuery(id+"F0.wireOp",EDGE,"E6"),sQuery(id+"F0.wireOp",EDGE,"E7"),sQuery(id+"F0.wireOp",EDGE,"E8"),sQuery(id+"F0.wireOp",EDGE,"E9"),sQuery(id+"F0.wireOp",EDGE,"E10")])]});
            var Q1;
            Q1=makeQuery(id+"F1.opExtrude","SWEPT_BODY",BODY,{"disambiguationData":[OSD([sQuery(id+"F0.wireOp",EDGE,"E2")])]});
            var Q2;
            Q2=makeQuery(id+"F1.opExtrude","SWEPT_BODY",BODY,{"disambiguationData":[OSD([sQuery(id+"F0.wireOp",EDGE,"E5")])]});
            var Q3;
            Q3=qCreatedBy(makeId("Origin.pointOp"),VERTEX);
            var Q4;
            Q4=qCreatedBy(makeId("Origin.pointOp"),VERTEX);
            transform(context, id + "F2", {"entities" : qUnion([Q0, Q1, Q2]), "transformType" : TransformType.SCALE_UNIFORMLY, "scale" : 0.5, "scalePoint" : qUnion([Q4]), "makeCopy" : false});
        }
    });
